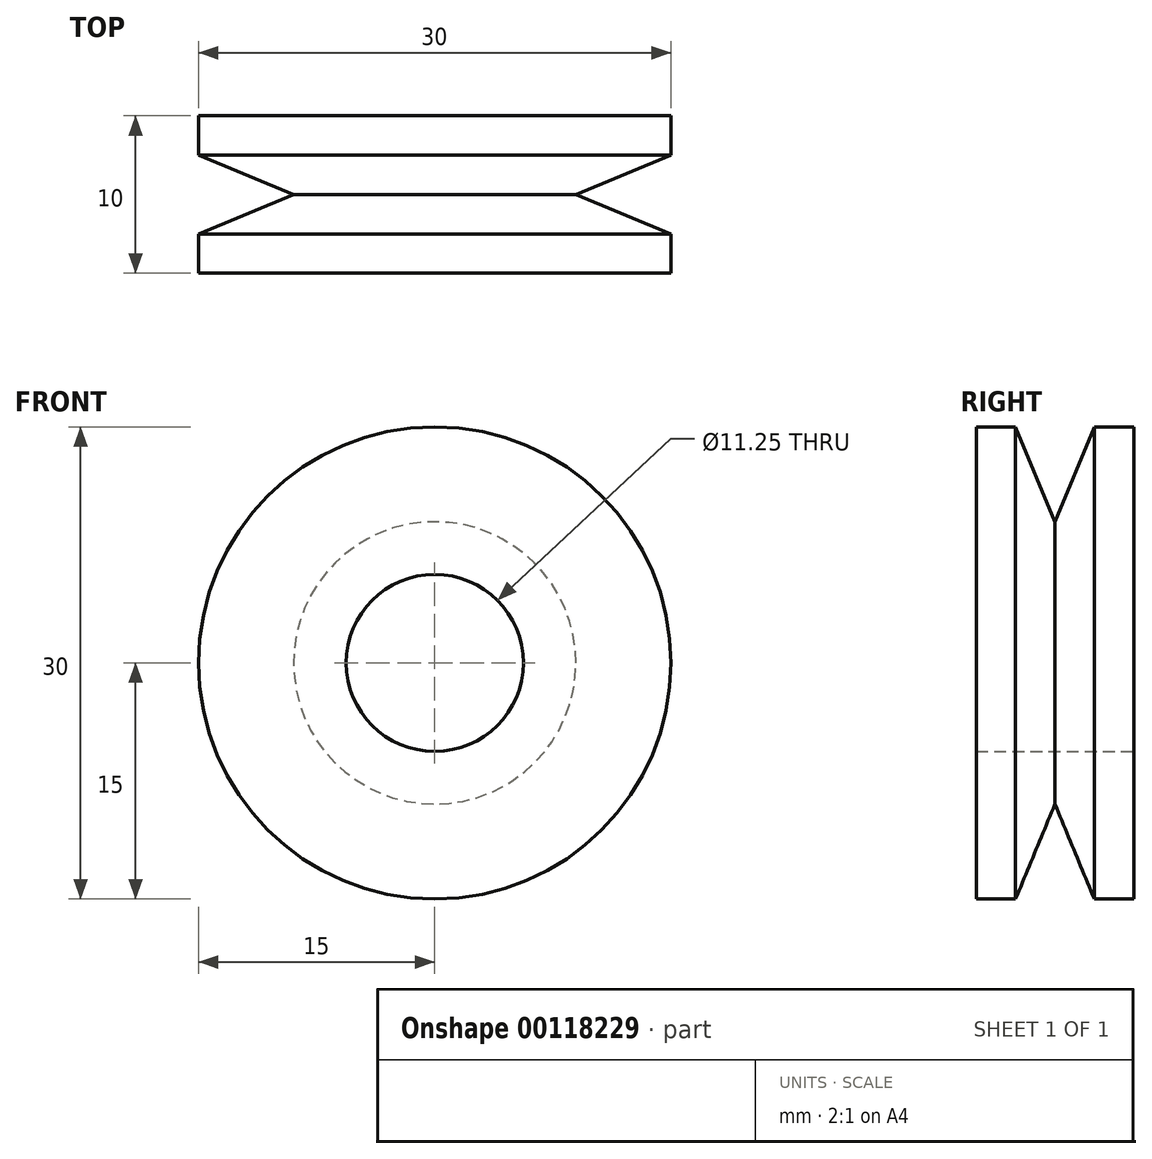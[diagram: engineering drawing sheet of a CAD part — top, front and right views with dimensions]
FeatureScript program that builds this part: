
annotation { "Feature Type Name" : "Feature", "Feature Type Description" : "" }
export const myFeature = defineFeature(function(context is Context, id is Id, definition is map)
    precondition{}
    {
        {
            var Q0;
            Q0=qCreatedBy(makeId("Front.planeOp"),FACE);
            var sketch = newSketch(context, id + "F0", { "sketchPlane" : qUnion([Q0])});
            skCircle(sketch, "E0", {"center": v(0, 0) * mm, "radius": 15 * mm});
            skCircle(sketch, "E1", {"center": v(0, 0) * mm, "radius": 5.62 * mm});
            skSolve(sketch);
        }
        {
            var Q0;
            Q0=makeQuery(id+"F0.imprint","IMPRINT",FACE,{"disambiguationData":[TD([[makeQuery(id+"F0.imprint","IMPRINT",EDGE,{"derivedFrom":sQuery(id+"F0.wireOp",EDGE,"E0")}),1.0]])]});
            extrude(context, id + "F1", {"entities" : qUnion([Q0]), "depth" : 10 * mm});
        }
        {
            var Q0;
            Q0=qCreatedBy(makeId("Right.planeOp"),FACE);
            cPlane(context, id + "F2", {"entities" : qUnion([Q0]), "cplaneType" : CPlaneType.OFFSET, "offset" : 0 * mm, "width" : 150 * mm, "height" : 150 * mm});
        }
        {
            var Q0;
            Q0=qCreatedBy(id+"F2.planeOp",FACE);
            var sketch = newSketch(context, id + "F3", { "sketchPlane" : qUnion([Q0])});
            skLineSegment(sketch, "E2", {"start": v(-7.5, 15) * mm, "end": v(-2.5, 15) * mm});
            skLineSegment(sketch, "E3", {"start": v(0, 15) * mm, "end": v(0, -15) * mm});
            skLineSegment(sketch, "E4", {"start": v(0, -15) * mm, "end": v(-10, -15) * mm});
            skLineSegment(sketch, "E5", {"start": v(-10, -15) * mm, "end": v(-10, 0) * mm});
            skLineSegment(sketch, "E6", {"start": v(-7.5, 15) * mm, "end": v(-5, 8.96) * mm});
            skLineSegment(sketch, "E7", {"start": v(-5, 8.96) * mm, "end": v(-2.5, 15) * mm});
            skPoint(sketch, "E8", {"position": v(-10, 0) * mm});
            skPoint(sketch, "E9.orphan", {"position": v(-10, 15) * mm});
            skSolve(sketch);
        }
        {
            var Q0;
            Q0 = qSketchRegion(id + "F3", true);
            var Q1;
            Q1=makeQuery(id+"F1.opExtrude","SWEPT_FACE",FACE,{"disambiguationData":[OSD([sQuery(id+"F0.wireOp",EDGE,"E1")])]});
            revolve(context, id + "F4", {"operationType" : NewBodyOperationType.REMOVE, "entities" : qUnion([Q0]), "axis" : qUnion([Q1]), "revolveType" : RevolveType.FULL, "oppositeDirection" : true});
        }
    });
